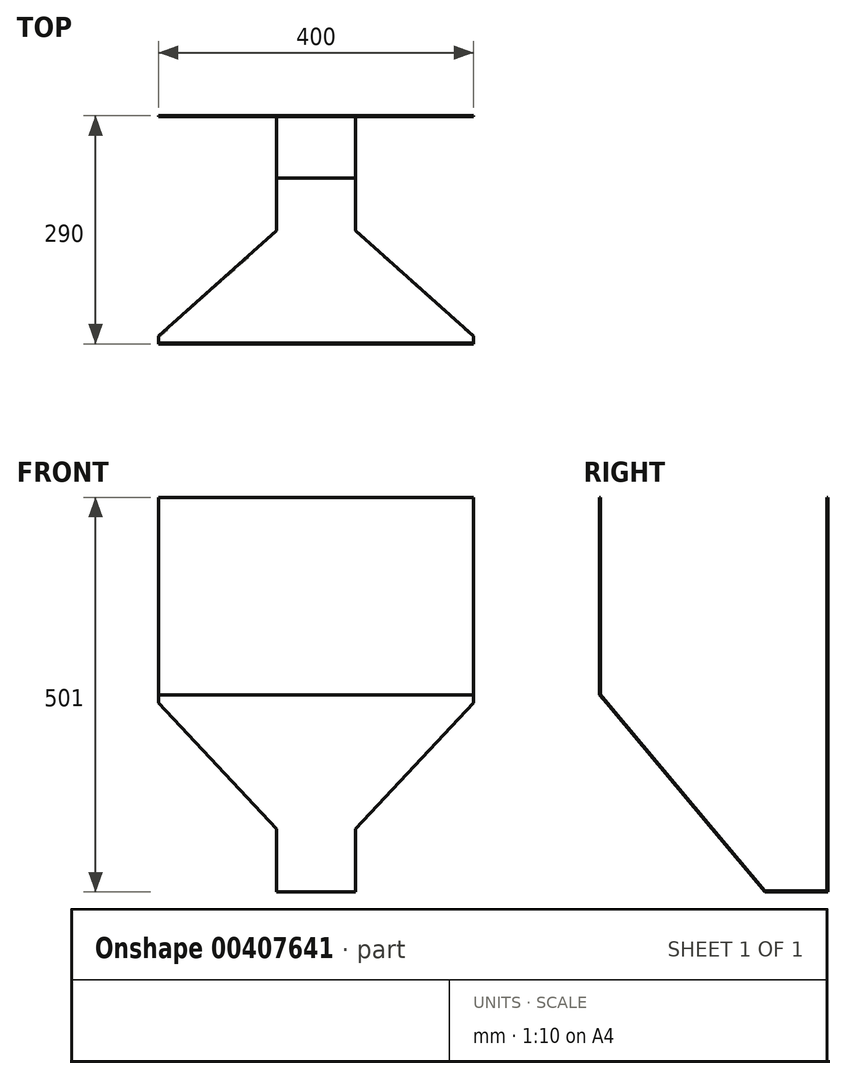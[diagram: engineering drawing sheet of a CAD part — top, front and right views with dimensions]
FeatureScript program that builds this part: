
annotation { "Feature Type Name" : "Feature", "Feature Type Description" : "" }
export const myFeature = defineFeature(function(context is Context, id is Id, definition is map)
    precondition{}
    {
        {
            var Q0;
            Q0=qCreatedBy(makeId("Right.planeOp"),FACE);
            var sketch = newSketch(context, id + "F0", { "sketchPlane" : qUnion([Q0])});
            skLineSegment(sketch, "E0", {"start": v(0, 0) * mm, "end": v(-80, 0) * mm});
            skLineSegment(sketch, "E1", {"start": v(-80, 0) * mm, "end": v(-290, 250.27) * mm});
            skLineSegment(sketch, "E2", {"start": v(-290, 250.27) * mm, "end": v(-290, 501) * mm});
            skLineSegment(sketch, "E3", {"start": v(0, 0) * mm, "end": v(0, 501) * mm});
            skLineSegment(sketch, "E4.0", {"start": v(-289, 250.63) * mm, "end": v(-289, 501) * mm});
            skLineSegment(sketch, "E4.1", {"start": v(-79.53, 1) * mm, "end": v(-289, 250.63) * mm});
            skLineSegment(sketch, "E4.2", {"start": v(-1, 1) * mm, "end": v(-79.53, 1) * mm});
            skLineSegment(sketch, "E4.3", {"start": v(-1, 1) * mm, "end": v(-1, 501) * mm});
            skLineSegment(sketch, "E5", {"start": v(-290, 501) * mm, "end": v(-289, 501) * mm});
            skLineSegment(sketch, "E6", {"start": v(-1, 501) * mm, "end": v(0, 501) * mm});
            skSolve(sketch);
        }
        {
            var Q0;
            Q0=makeQuery(id+"F0.imprint","IMPRINT",FACE,{"disambiguationData":[TD([[makeQuery(id+"F0.imprint","IMPRINT",EDGE,{"derivedFrom":sQuery(id+"F0.wireOp",EDGE,"E0")}),-1.0]])]});
            extrude(context, id + "F1", {"entities" : qUnion([Q0]), "oppositeDirection" : true, "depth" : 400 * mm});
        }
        {
            var Q0;
            Q0=makeQuery(id+"F1.opExtrude","SWEPT_FACE",FACE,{"disambiguationData":[OSD([sQuery(id+"F0.wireOp",EDGE,"E3")])]});
            var sketch = newSketch(context, id + "F2", { "sketchPlane" : qUnion([Q0])});
            skLineSegment(sketch, "E7", {"start": v(400, 240) * mm, "end": v(250, 80) * mm});
            skLineSegment(sketch, "E8", {"start": v(250, 80) * mm, "end": v(250, 0) * mm});
            skLineSegment(sketch, "E9", {"start": v(200, 0) * mm, "end": v(200, 198.96) * mm, "construction": true});
            skLineSegment(sketch, "E10.MirrorCS", {"start": v(0, 240) * mm, "end": v(150, 80) * mm});
            skLineSegment(sketch, "E11.MirrorCS", {"start": v(150, 80) * mm, "end": v(150, 0) * mm});
            skSolve(sketch);
        }
        {
            var Q0;
            {var subQ0=sQuery(id+"F2.wireOp",EDGE,"Qxc1O4Ee-7d8E-R3Kk-48Ti-2GcufYxCDCyJ");Q0=makeQuery(id+"F2.imprint","IMPRINT",FACE,{"disambiguationData":[TD([[makeQuery(id+"F2.imprint","IMPRINT",EDGE,{"derivedFrom":subQ0}),-1.0]])]});}
            var Q1;
            {var subQ0=sQuery(id+"F2.wireOp",EDGE,"E7");Q1=makeQuery(id+"F2.imprint","IMPRINT",FACE,{"disambiguationData":[TD([[makeQuery(id+"F2.imprint","IMPRINT",EDGE,{"derivedFrom":subQ0}),1.0]])]});}
            var Q2;
            {var subQ0=sQuery(id+"F2.wireOp",EDGE,"E10.MirrorCS");Q2=makeQuery(id+"F2.imprint","IMPRINT",FACE,{"disambiguationData":[TD([[makeQuery(id+"F2.imprint","IMPRINT",EDGE,{"derivedFrom":subQ0}),-1.0]])]});}
            extrude(context, id + "F3", {"entities" : qUnion([Q0, Q1, Q2]), "operationType" : NewBodyOperationType.REMOVE, "endBound" : BoundingType.THROUGH_ALL, "oppositeDirection" : true, "depth" : 25 * mm});
        }
    });
